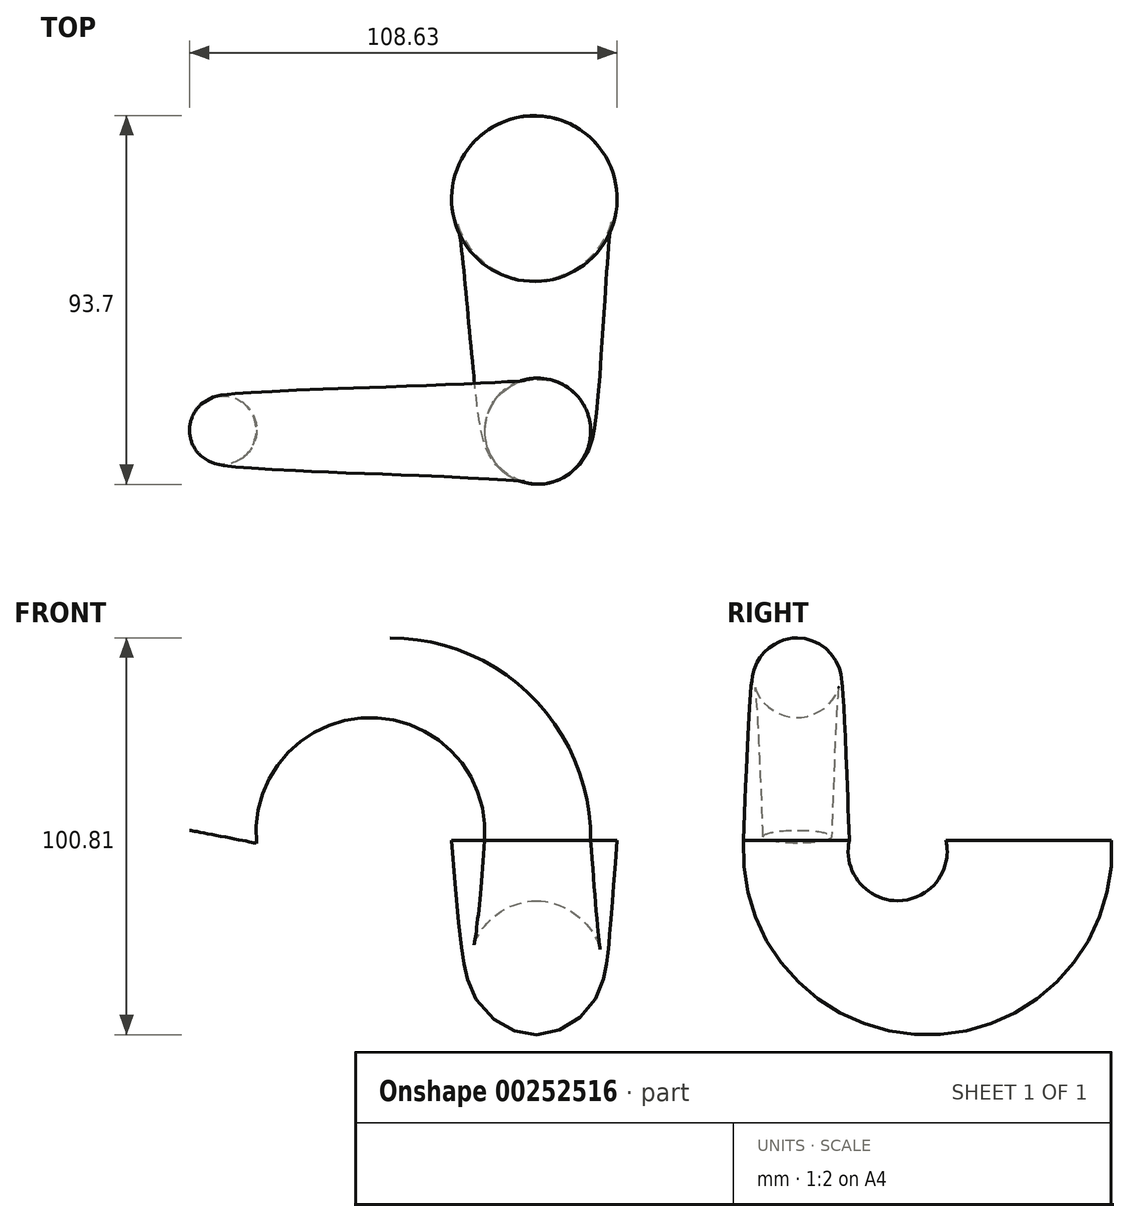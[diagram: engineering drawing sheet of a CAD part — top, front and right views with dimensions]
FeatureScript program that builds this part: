
annotation { "Feature Type Name" : "Feature", "Feature Type Description" : "" }
export const myFeature = defineFeature(function(context is Context, id is Id, definition is map)
    precondition{}
    {
        {
            var Q0;
            Q0=qCreatedBy(makeId("Front.planeOp"),FACE);
            var sketch = newSketch(context, id + "F0", { "sketchPlane" : qUnion([Q0])});
            skArc(sketch, "E0", {"start": v(38.69, 11.88) * mm, "mid": v(-0.44, 45.36) * mm, "end": v(-40.38, 12.85) * mm});
            skSolve(sketch);
        }
        {
            var Q0;
            Q0=qCreatedBy(makeId("Right.planeOp"),FACE);
            var Q1;
            Q1=sQuery(id+"F0.wireOp",VERTEX,"E0.start");
            cPlane(context, id + "F1", {"entities" : qUnion([Q0, Q1]), "cplaneType" : CPlaneType.PLANE_POINT, "offset" : 25.4 * mm, "width" : 152.4 * mm, "height" : 152.4 * mm});
        }
        {
            var Q0;
            Q0=qCreatedBy(id+"F1.planeOp",FACE);
            var sketch = newSketch(context, id + "F2", { "sketchPlane" : qUnion([Q0])});
            skPoint(sketch, "E1.0", {"position": v(0, 11.88) * mm});
            skArc(sketch, "E2", {"start": v(0, 11.88) * mm, "mid": v(29.4, -17.52) * mm, "end": v(58.8, 11.88) * mm});
            skSolve(sketch);
        }
        {
            var Q0;
            Q0=sQuery(id+"F2.wireOp",VERTEX,"E2.end");
            var Q1;
            Q1=sQuery(id+"F2.wireOp",EDGE,"E2");
            cPlane(context, id + "F3", {"entities" : qUnion([Q0, Q1]), "cplaneType" : CPlaneType.CURVE_POINT, "offset" : 25.4 * mm, "width" : 152.4 * mm, "height" : 152.4 * mm});
        }
        {
            var Q0;
            Q0=sQuery(id+"F0.wireOp",VERTEX,"E0.end");
            var Q1;
            Q1=sQuery(id+"F0.wireOp",EDGE,"E0");
            cPlane(context, id + "F4", {"entities" : qUnion([Q0, Q1]), "cplaneType" : CPlaneType.CURVE_POINT, "offset" : 25.4 * mm, "width" : 152.4 * mm, "height" : 152.4 * mm});
        }
        {
            var Q0;
            Q0=qCreatedBy(id+"F3.planeOp",FACE);
            var sketch = newSketch(context, id + "F5", { "sketchPlane" : qUnion([Q0])});
            skPoint(sketch, "E3.0", {"position": v(38.69, 58.8) * mm});
            skCircle(sketch, "E4", {"center": v(38.69, 58.8) * mm, "radius": 21.03 * mm});
            skPoint(sketch, "E5", {"position": v(17.66, 59.54) * mm});
            skPoint(sketch, "E6.end.orphan", {"position": v(59.72, 58.8) * mm});
            skSolve(sketch);
        }
        {
            var Q0;
            Q0=qCreatedBy(id+"F4.planeOp",FACE);
            var sketch = newSketch(context, id + "F6", { "sketchPlane" : qUnion([Q0])});
            skPoint(sketch, "E7.0", {"position": v(-42.1, 0) * mm});
            skCircle(sketch, "E8", {"center": v(-42.1, 0) * mm, "radius": 8.69 * mm});
            skSolve(sketch);
        }
        {
            var Q0;
            Q0=qCreatedBy(makeId("Front.planeOp"),FACE);
            var sketch = newSketch(context, id + "F7", { "sketchPlane" : qUnion([Q0])});
            skLineSegment(sketch, "E9.0", {"start": v(-31.86, 11.2) * mm, "end": v(-48.91, 14.51) * mm});
            skLineSegment(sketch, "E10.0", {"start": v(17.65, 11.88) * mm, "end": v(59.72, 11.88) * mm});
            skFitSpline(sketch, "E11", {"points": [v(-48.91, 14.51) * mm, v(-33.83, 45.11) * mm, v(14.43, 53.6) * mm, v(42.08, 32.26) * mm, v(53, 11.88) * mm], "startDerivative": vector(33.1, 139.02) * mm, "endDerivative": vector(44.58, -98.17) * mm});
            skFitSpline(sketch, "E12", {"points": [v(-31.86, 11.2) * mm, v(-25.1, 25.22) * mm, v(-6.43, 37.84) * mm, v(14.92, 31.29) * mm, v(26.07, 11.88) * mm], "startDerivative": vector(22.52, 64.52) * mm, "endDerivative": vector(32.33, -82.7) * mm});
            skArc(sketch, "E13", {"start": v(53, 11.88) * mm, "mid": v(3.34, 63.35) * mm, "end": v(-48.91, 14.51) * mm});
            skArc(sketch, "E14", {"start": v(26.07, 11.88) * mm, "mid": v(-3.27, 43.12) * mm, "end": v(-31.86, 11.2) * mm});
            skSolve(sketch);
        }
        {
            var Q0;
            Q0=qCreatedBy(id+"F3.planeOp",FACE);
            var sketch = newSketch(context, id + "F8", { "sketchPlane" : qUnion([Q0])});
            skCircle(sketch, "E15.0", {"center": v(38.69, 58.8) * mm, "radius": 21.03 * mm});
            skPoint(sketch, "E15.1", {"position": v(53, 0) * mm});
            skPoint(sketch, "E15.2", {"position": v(26.07, 0) * mm});
            skLineSegment(sketch, "E16", {"start": v(53, 0) * mm, "end": v(59.72, 58.8) * mm});
            skLineSegment(sketch, "E17", {"start": v(26.07, 0) * mm, "end": v(17.66, 59.54) * mm});
            skCircle(sketch, "E18", {"center": v(39.53, -0.26) * mm, "radius": 13.46 * mm});
            skPoint(sketch, "E18.third.point", {"position": v(35.24, -13.02) * mm});
            skLineSegment(sketch, "E19", {"start": v(38.99, 37.77) * mm, "end": v(39.34, 13.2) * mm});
            skLineSegment(sketch, "E20", {"start": v(38.38, 79.84) * mm, "end": v(39.34, 13.2) * mm});
            skSolve(sketch);
        }
        {
            var Q0;
            Q0=makeQuery(id+"F6.imprint","IMPRINT",FACE,{"disambiguationData":[TD([[makeQuery(id+"F6.imprint","IMPRINT",EDGE,{"derivedFrom":sQuery(id+"F6.wireOp",EDGE,"E8")}),1.0]])]});
            var Q1;
            {var subQ0=sQuery(id+"F8.wireOp",EDGE,"E18");var subQ1=makeQuery(id+"F8.imprint","INTERSECT",VERTEX,{"derivedFrom":[sQuery(id+"F8.wireOp",EDGE,"E16"),subQ0]});Q1=makeQuery(id+"F8.imprint","IMPRINT",FACE,{"disambiguationData":[TD([[makeQuery(id+"F8.imprint","IMPRINT",EDGE,{"disambiguationData":[TD([[subQ1,-1.0]])],"derivedFrom":subQ0}),1.0]])]});}
            var Q2;
            Q2=sQuery(id+"F7.wireOp",EDGE,"E13");
            var Q3;
            Q3=sQuery(id+"F7.wireOp",EDGE,"E14");
            loft(context, id + "F9", {"addGuides" : true, "sheetProfilesArray" : [{ "sheetProfileEntities" : qUnion([Q0]) }, { "sheetProfileEntities" : qUnion([Q1]) }], "guidesArray" : [{ "guideEntities" : qUnion([Q2]), "guideDerivativeType" : LoftGuideDerivativeType.DEFAULT, "guideDerivativeMagnitude" : 1 }, { "guideEntities" : qUnion([Q3]), "guideDerivativeType" : LoftGuideDerivativeType.DEFAULT, "guideDerivativeMagnitude" : 1 }]});
        }
        {
            var Q0;
            Q0=sQuery(id+"F8.wireOp",EDGE,"E20");
            cPlane(context, id + "F10", {"entities" : qUnion([Q0]), "cplaneType" : CPlaneType.LINE_ANGLE, "offset" : 25.4 * mm, "angle" : 90 * degree, "width" : 152.4 * mm, "height" : 152.4 * mm});
        }
        {
            var Q0;
            Q0=qCreatedBy(id+"F10.planeOp",FACE);
            var sketch = newSketch(context, id + "F11", { "sketchPlane" : qUnion([Q0])});
            skLineSegment(sketch, "E21.0", {"start": v(-14.29, 11.88) * mm, "end": v(12.64, 11.88) * mm});
            skLineSegment(sketch, "E21.1", {"start": v(37.2, 11.88) * mm, "end": v(79.28, 11.88) * mm});
            skArc(sketch, "E22", {"start": v(-14.29, 11.88) * mm, "mid": v(32.5, -23.58) * mm, "end": v(79.28, 11.88) * mm});
            skArc(sketch, "E23", {"start": v(12.64, 11.88) * mm, "mid": v(24.92, -3.42) * mm, "end": v(37.2, 11.88) * mm});
            skArc(sketch, "E24", {"start": v(-14.29, 11.88) * mm, "mid": v(32.5, -37.47) * mm, "end": v(79.28, 11.88) * mm});
            skSolve(sketch);
        }
        {
            var Q0;
            {var subQ0=sQuery(id+"F8.wireOp",EDGE,"E18");var subQ1=makeQuery(id+"F8.imprint","INTERSECT",VERTEX,{"derivedFrom":[sQuery(id+"F8.wireOp",EDGE,"E16"),subQ0]});Q0=makeQuery(id+"F8.imprint","IMPRINT",FACE,{"disambiguationData":[TD([[makeQuery(id+"F8.imprint","IMPRINT",EDGE,{"disambiguationData":[TD([[subQ1,-1.0]])],"derivedFrom":subQ0}),1.0]])]});}
            var Q1;
            Q1=makeQuery(id+"F5.imprint","IMPRINT",FACE,{"disambiguationData":[TD([[makeQuery(id+"F5.imprint","IMPRINT",EDGE,{"derivedFrom":sQuery(id+"F5.wireOp",EDGE,"E4")}),1.0]])]});
            var Q2;
            Q2=sQuery(id+"F11.wireOp",EDGE,"E23");
            var Q3;
            Q3=sQuery(id+"F11.wireOp",EDGE,"E24");
            loft(context, id + "F12", {"addGuides" : true, "sheetProfilesArray" : [{ "sheetProfileEntities" : qUnion([Q0]) }, { "sheetProfileEntities" : qUnion([Q1]) }], "guidesArray" : [{ "guideEntities" : qUnion([Q2]), "guideDerivativeType" : LoftGuideDerivativeType.DEFAULT, "guideDerivativeMagnitude" : 1 }, { "guideEntities" : qUnion([Q3]), "guideDerivativeType" : LoftGuideDerivativeType.DEFAULT, "guideDerivativeMagnitude" : 1 }]});
        }
    });
